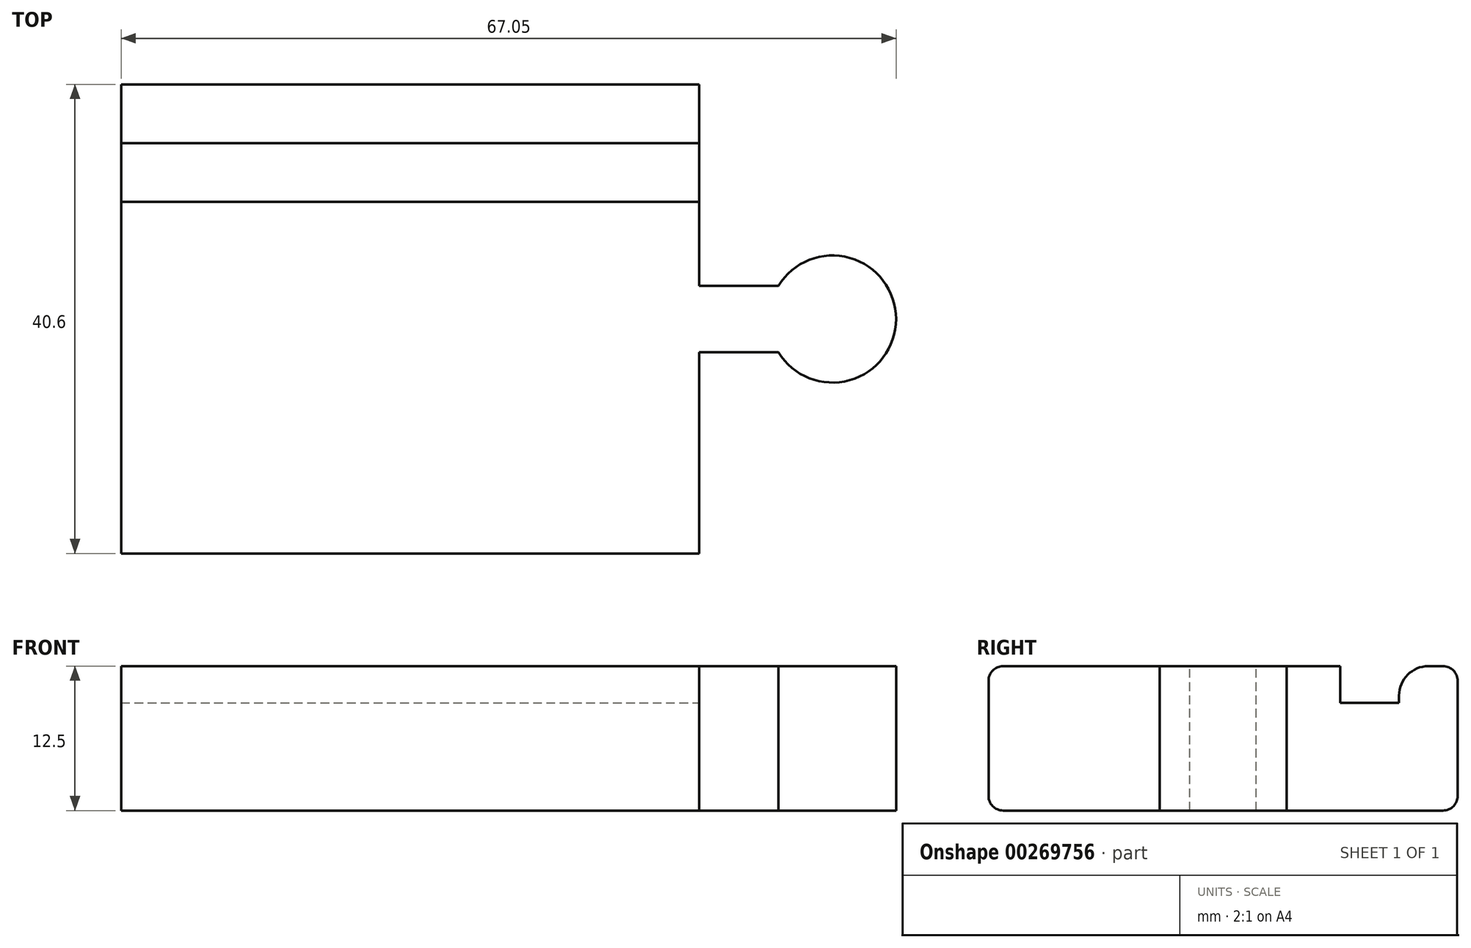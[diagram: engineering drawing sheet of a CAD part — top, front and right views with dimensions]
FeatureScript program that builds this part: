
annotation { "Feature Type Name" : "Feature", "Feature Type Description" : "" }
export const myFeature = defineFeature(function(context is Context, id is Id, definition is map)
    precondition{}
    {
        {
            var Q0;
            Q0=qCreatedBy(makeId("Top.planeOp"),FACE);
            var sketch = newSketch(context, id + "F0", { "sketchPlane" : qUnion([Q0])});
            skLineSegment(sketch, "E0.bottom", {"start": v(25, 20.3) * mm, "end": v(-25, 20.3) * mm});
            skLineSegment(sketch, "E0.top", {"start": v(25, -20.3) * mm, "end": v(-25, -20.3) * mm});
            skLineSegment(sketch, "E0.left", {"start": v(25, 20.3) * mm, "end": v(25, -20.3) * mm});
            skLineSegment(sketch, "E0.right", {"start": v(-25, 20.3) * mm, "end": v(-25, -20.3) * mm});
            skPoint(sketch, "E0.middle", {"position": v(0, 0) * mm});
            skSolve(sketch);
        }
        {
            var Q0;
            Q0 = qSketchRegion(id + "F0", true);
            extrude(context, id + "F1", {"entities" : qUnion([Q0]), "depth" : 12.5 * mm});
        }
        {
            var Q0;
            Q0=makeQuery(id+"F1.opExtrude","CAP_FACE",FACE,{"disambiguationData":[OSD([sQuery(id+"F0.wireOp",EDGE,"E0.bottom"),sQuery(id+"F0.wireOp",EDGE,"E0.top"),sQuery(id+"F0.wireOp",EDGE,"E0.left"),sQuery(id+"F0.wireOp",EDGE,"E0.right")])],"isStart":false});
            var sketch = newSketch(context, id + "F2", { "sketchPlane" : qUnion([Q0])});
            skLineSegment(sketch, "E1", {"start": v(25, 0) * mm, "end": v(36.55, 0) * mm, "construction": true});
            skPoint(sketch, "E1.endSnap0", {"position": v(25, 0) * mm});
            skArc(sketch, "E2", {"start": v(31.86, -2.88) * mm, "mid": v(42.05, 0) * mm, "end": v(31.86, 2.87) * mm});
            skLineSegment(sketch, "E3", {"start": v(25, 0) * mm, "end": v(25, 2.87) * mm});
            skLineSegment(sketch, "E4", {"start": v(25, 2.87) * mm, "end": v(31.86, 2.87) * mm});
            skLineSegment(sketch, "E5", {"start": v(25, 0) * mm, "end": v(25, -2.88) * mm});
            skLineSegment(sketch, "E6", {"start": v(25, -2.88) * mm, "end": v(31.86, -2.88) * mm});
            skSolve(sketch);
        }
        {
            var Q0;
            Q0 = qSketchRegion(id + "F2", true);
            var Q1;
            Q1=makeQuery(id+"F1.opExtrude","CAP_FACE",FACE,{"disambiguationData":[OSD([sQuery(id+"F0.wireOp",EDGE,"E0.bottom"),sQuery(id+"F0.wireOp",EDGE,"E0.top"),sQuery(id+"F0.wireOp",EDGE,"E0.left"),sQuery(id+"F0.wireOp",EDGE,"E0.right")])],"isStart":true});
            extrude(context, id + "F3", {"entities" : qUnion([Q0]), "operationType" : NewBodyOperationType.ADD, "endBound" : BoundingType.UP_TO_SURFACE, "oppositeDirection" : true, "endBoundEntityFace" : qUnion([Q1]), "depth" : 12 * mm});
        }
        {
            var Q0;
            {var subQ0=sQuery(id+"F2.wireOp",EDGE,"kprsDvC4-vMBq-rOdD-pwMV-9uyCiIca7NPs.right");var subQ1=sQuery(id+"F2.wireOp",EDGE,"kprsDvC4-vMBq-rOdD-pwMV-9uyCiIca7NPs.top");var subQ2=sQuery(id+"F2.wireOp",EDGE,"kprsDvC4-vMBq-rOdD-pwMV-9uyCiIca7NPs.bottom");var subQ3=sQuery(id+"F2.wireOp",EDGE,"Drm0USrt-R8gS-Y0M4-SWiu-MueqH25JkZSp");Q0=makeQuery(id+"Fgbf0bgwTR2DJ2I_1.1.F3.boolean.opBoolean","MERGE",FACE,{"derivedFrom":[makeQuery(id+"F3.boolean.opBoolean","MERGE",FACE,{"derivedFrom":[makeQuery(id+"F1.opExtrude","CAP_FACE",FACE,{"disambiguationData":[OSD([sQuery(id+"F0.wireOp",EDGE,"E0.bottom"),sQuery(id+"F0.wireOp",EDGE,"E0.top"),sQuery(id+"F0.wireOp",EDGE,"E0.left"),sQuery(id+"F0.wireOp",EDGE,"E0.right")])],"isStart":false}),makeQuery(id+"F3.opExtrude","CAP_FACE",FACE,{"disambiguationData":[OSD([subQ3,subQ2,subQ1,subQ0])],"isStart":false})]}),makeQuery(id+"Fgbf0bgwTR2DJ2I_1.1.F3.opExtrude","CAP_FACE",FACE,{"disambiguationData":[OSD([subQ3,subQ2,subQ1,subQ0])],"isStart":false})]});}
            var sketch = newSketch(context, id + "F4", { "sketchPlane" : qUnion([Q0])});
            skLineSegment(sketch, "E7.bottom", {"start": v(-25, 15.22) * mm, "end": v(25, 15.22) * mm});
            skLineSegment(sketch, "E7.top", {"start": v(-25, 10.14) * mm, "end": v(25, 10.14) * mm});
            skLineSegment(sketch, "E7.left", {"start": v(-25, 15.22) * mm, "end": v(-25, 10.14) * mm});
            skLineSegment(sketch, "E7.right", {"start": v(25, 15.22) * mm, "end": v(25, 10.14) * mm});
            skSolve(sketch);
        }
        {
            var Q0;
            Q0 = qSketchRegion(id + "F4", true);
            extrude(context, id + "F5", {"entities" : qUnion([Q0]), "operationType" : NewBodyOperationType.REMOVE, "oppositeDirection" : true, "depth" : 3.17 * mm});
        }
        {
            var Q0;
            Q0=makeQuery(id+"F1.opExtrude","CAP_EDGE",EDGE,{"disambiguationData":[OSD([sQuery(id+"F0.wireOp",EDGE,"E0.bottom")])],"isStart":false});
            var Q1;
            Q1=makeQuery(id+"F1.opExtrude","CAP_EDGE",EDGE,{"disambiguationData":[OSD([sQuery(id+"F0.wireOp",EDGE,"E0.top")])],"isStart":false});
            var Q2;
            Q2=makeQuery(id+"F1.opExtrude","CAP_EDGE",EDGE,{"disambiguationData":[OSD([sQuery(id+"F0.wireOp",EDGE,"E0.bottom")])],"isStart":true});
            var Q3;
            Q3=makeQuery(id+"F1.opExtrude","CAP_EDGE",EDGE,{"disambiguationData":[OSD([sQuery(id+"F0.wireOp",EDGE,"E0.top")])],"isStart":true});
            fillet(context, id + "F6", {"entities" : qUnion([Q0, Q1, Q2, Q3]), "radius" : 1.27 * mm, "tangentPropagation" : true, "allowEdgeOverflow" : false});
        }
        {
            var Q0;
            Q0=makeQuery(id+"F5.boolean.opBoolean","COPY",EDGE,{"derivedFrom":makeQuery(id+"F5.opExtrude","CAP_EDGE",EDGE,{"disambiguationData":[OSD([sQuery(id+"F4.wireOp",EDGE,"E7.bottom")])],"isStart":true})});
            var Q1;
            Q1=makeQuery(id+"F5.boolean.opBoolean","COPY",EDGE,{"derivedFrom":makeQuery(id+"F5.opExtrude","CAP_EDGE",EDGE,{"disambiguationData":[OSD([sQuery(id+"F4.wireOp",EDGE,"E7.top")])],"isStart":true})});
            fillet(context, id + "F7", {"entities" : qUnion([Q0, Q1]), "radius" : 2.54 * mm, "tangentPropagation" : true, "allowEdgeOverflow" : false});
        }
    });
